# Revit family: Wall-Spout_Traditional_Guinevere_TS970E_TOTO
name_source: partatom
category: Plumbing Fixtures
revit_build: Autodesk Revit Architecture 2013 (Build: 20130531_2115(x64)
units: mm (PartAtom-declared; Revit-internal decimal feet)

## types (1)
- TS970E
    04 CSI = 22 41 39
    95 CSI = 15416
    ADA Compliant = No
    Apparent Power = 0 VA
    Assembly Code = D2010
    CAD Drawing URL = http://assets.totousa.com
    CW Connection = Yes
    CWFU = 0
    Color Availability = #CP Polished Chrome, #BN Brushed Nickel, #PN Polished Nickel, #RB Oil Rubbed Bronze
    Current = 0 A
    Default Elevation = 31"
    Depth = 7"
    Description = Wall Spout
    Finish = Metal - TOTO - LifeKoat - Nickel - Brushed
    Flow Pressure = 0.00 psi
    Flow Rate = 0 GPM
    Frequency = 0 Hz
    HW Connection = Yes
    HWFU = 0
    Height = 2 1/4"
    Hot Water Connection NPT Radius = 0"
    Manufacturer = TOTO USA, Inc.
    Manufacturer Fax = (770) 282-0002
    Model = TS970E
    Number of Poles = 1
    Series = Guinevere
    Shipping Weight = 3.00 lb
    Spec Sheet URL = http://assets.totousa.com
    Style = Traditional
    Subcategory = Showers
    Tempered Water Connection Radius = 0"
    Toto BIM Number = BM-00173
    URL = http://www.totousa.com
    Vent Connection = No
    Voltage = 0 V
    WFU = 0
    Warranty = Lifetime Limited Warranty (Residential Use); One Year (Oil Rubbed Bronze); One Year Limited (Commercial Use)
    Warranty URL = http://www.totousa.com
    Waste Connection = No
    Waste Connection Radius = 0"
    Water Connection Radius = 1/4"
    Width = 2 1/16"

## geometry (parser evidence)
native form markers: Blend x24, Sweep x1
no freeform markers — native parametric forms only
